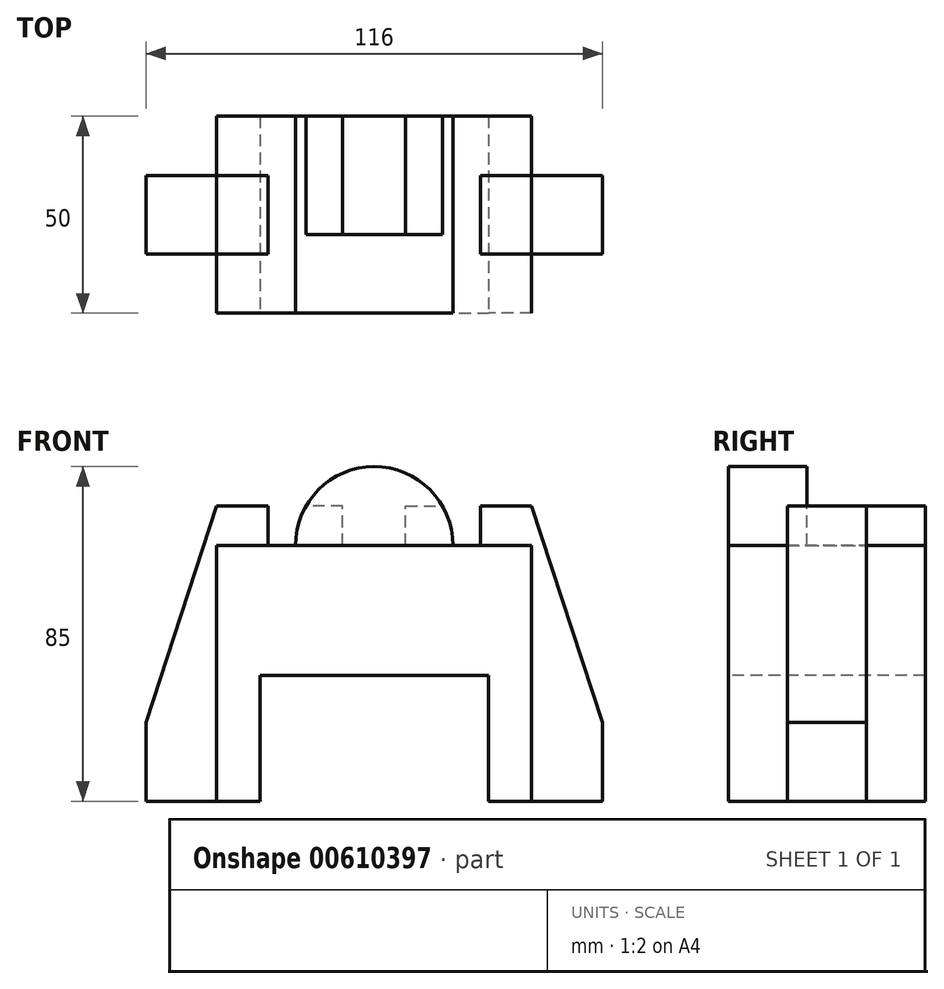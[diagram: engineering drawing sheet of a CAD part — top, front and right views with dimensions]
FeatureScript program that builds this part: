
annotation { "Feature Type Name" : "Feature", "Feature Type Description" : "" }
export const myFeature = defineFeature(function(context is Context, id is Id, definition is map)
    precondition{}
    {
        {
            var Q0;
            Q0=qCreatedBy(makeId("Top.planeOp"),FACE);
            var sketch = newSketch(context, id + "F0", { "sketchPlane" : qUnion([Q0])});
            skLineSegment(sketch, "E0.bottom", {"start": v(40, 25) * mm, "end": v(-40, 25) * mm});
            skLineSegment(sketch, "E0.top", {"start": v(40, -25) * mm, "end": v(-40, -25) * mm});
            skLineSegment(sketch, "E0.left", {"start": v(40, 25) * mm, "end": v(40, -25) * mm});
            skLineSegment(sketch, "E0.right", {"start": v(-40, 25) * mm, "end": v(-40, -25) * mm});
            skPoint(sketch, "E0.middle", {"position": v(0, 0) * mm});
            skSolve(sketch);
        }
        {
            var Q0;
            Q0 = qSketchRegion(id + "F0", true);
            extrude(context, id + "F1", {"entities" : qUnion([Q0]), "depth" : 65 * mm, "offsetDistance" : 25 * mm});
        }
        {
            var Q0;
            Q0=makeQuery(id+"F1.opExtrude","SWEPT_FACE",FACE,{"disambiguationData":[OSD([sQuery(id+"F0.wireOp",EDGE,"E0.top")])]});
            var sketch = newSketch(context, id + "F2", { "sketchPlane" : qUnion([Q0])});
            skLineSegment(sketch, "E1", {"start": v(0, 0) * mm, "end": v(29, 0) * mm});
            skLineSegment(sketch, "E2", {"start": v(29, 0) * mm, "end": v(-29, 0) * mm});
            skLineSegment(sketch, "E3", {"start": v(-29, 0) * mm, "end": v(-29, 32) * mm});
            skLineSegment(sketch, "E4", {"start": v(-29, 32) * mm, "end": v(29, 32) * mm});
            skLineSegment(sketch, "E5", {"start": v(29, 32) * mm, "end": v(29, 0) * mm});
            skSolve(sketch);
        }
        {
            var Q0;
            Q0 = qSketchRegion(id + "F2", true);
            extrude(context, id + "F3", {"entities" : qUnion([Q0]), "operationType" : NewBodyOperationType.REMOVE, "oppositeDirection" : true, "depth" : 234.7 * mm, "offsetDistance" : 25 * mm});
        }
        {
            var Q0;
            Q0=makeQuery(id+"F1.opExtrude","SWEPT_FACE",FACE,{"disambiguationData":[OSD([sQuery(id+"F0.wireOp",EDGE,"E0.top")])]});
            var sketch = newSketch(context, id + "F4", { "sketchPlane" : qUnion([Q0])});
            skArc(sketch, "E6", {"start": v(20, 65) * mm, "mid": v(0, 85) * mm, "end": v(-20, 65) * mm});
            skLineSegment(sketch, "E7", {"start": v(-36.6, 65) * mm, "end": v(34.21, 65) * mm});
            skSolve(sketch);
        }
        {
            var Q0;
            {var subQ0=sQuery(id+"F4.wireOp",EDGE,"E6");Q0=makeQuery(id+"F4.imprint","IMPRINT",FACE,{"disambiguationData":[TD([[makeQuery(id+"F4.imprint","IMPRINT",EDGE,{"derivedFrom":subQ0}),1.0]])]});}
            var Q1;
            Q1=makeQuery(id+"F1.opExtrude","SWEPT_FACE",FACE,{"disambiguationData":[OSD([sQuery(id+"F0.wireOp",EDGE,"E0.bottom")])]});
            extrude(context, id + "F5", {"entities" : qUnion([Q0]), "endBound" : BoundingType.UP_TO_SURFACE, "oppositeDirection" : true, "depth" : 25 * mm, "endBoundEntityFace" : qUnion([Q1]), "offsetDistance" : 25 * mm});
        }
        {
            var Q0;
            Q0=makeQuery(id+"F5.opExtrude","CAP_FACE",FACE,{"disambiguationData":[OSD([sQuery(id+"F4.wireOp",EDGE,"E6"),sQuery(id+"F4.wireOp",EDGE,"E7")])],"isStart":false});
            var sketch = newSketch(context, id + "F6", { "sketchPlane" : qUnion([Q0])});
            skLineSegment(sketch, "E8", {"start": v(0, 65) * mm, "end": v(8, 65) * mm});
            skLineSegment(sketch, "E9", {"start": v(8, 65) * mm, "end": v(-8, 65) * mm});
            skLineSegment(sketch, "E10", {"start": v(-8, 65) * mm, "end": v(-8, 75) * mm});
            skLineSegment(sketch, "E11", {"start": v(-8, 75) * mm, "end": v(-17.32, 75) * mm});
            skLineSegment(sketch, "E12", {"start": v(8, 65) * mm, "end": v(8, 75) * mm});
            skLineSegment(sketch, "E13", {"start": v(8, 75) * mm, "end": v(17.32, 75) * mm});
            skLineSegment(sketch, "E14", {"start": v(-8, 75) * mm, "end": v(8, 75) * mm});
            skSolve(sketch);
        }
        {
            var Q0;
            {var subQ0=sQuery(id+"F6.wireOp",EDGE,"E11");Q0=makeQuery(id+"F6.imprint","IMPRINT",FACE,{"disambiguationData":[TD([[makeQuery(id+"F6.imprint","IMPRINT",EDGE,{"derivedFrom":subQ0}),-1.0]])]});}
            var Q1;
            {var subQ5=sQuery(id+"F6.wireOp",EDGE,"E10");Q1=makeQuery(id+"F6.imprint","IMPRINT",FACE,{"disambiguationData":[TD([[makeQuery(id+"F6.imprint","IMPRINT",EDGE,{"derivedFrom":subQ5}),-1.0]])]});}
            extrude(context, id + "F7", {"entities" : qUnion([Q0, Q1]), "operationType" : NewBodyOperationType.REMOVE, "oppositeDirection" : true, "depth" : 30 * mm, "offsetDistance" : 25 * mm});
        }
        {
            var Q0;
            Q0=qCreatedBy(makeId("Front.planeOp"),FACE);
            var sketch = newSketch(context, id + "F8", { "sketchPlane" : qUnion([Q0])});
            skLineSegment(sketch, "E15.0.0", {"start": v(29, 0) * mm, "end": v(29, 32) * mm});
            skLineSegment(sketch, "E15.0.1", {"start": v(29, 32) * mm, "end": v(-29, 32) * mm});
            skLineSegment(sketch, "E15.0.2", {"start": v(-29, 32) * mm, "end": v(-29, 0) * mm});
            skLineSegment(sketch, "E15.0.3", {"start": v(-29, 0) * mm, "end": v(-40, 0) * mm});
            skLineSegment(sketch, "E15.0.4", {"start": v(-40, 0) * mm, "end": v(-40, 65) * mm});
            skLineSegment(sketch, "E15.0.5", {"start": v(-40, 65) * mm, "end": v(40, 65) * mm});
            skLineSegment(sketch, "E15.0.6", {"start": v(40, 65) * mm, "end": v(40, 0) * mm});
            skLineSegment(sketch, "E15.0.7", {"start": v(40, 0) * mm, "end": v(29, 0) * mm});
            skLineSegment(sketch, "E16", {"start": v(40, 0) * mm, "end": v(58, 0) * mm});
            skLineSegment(sketch, "E17", {"start": v(40, 65) * mm, "end": v(27, 65) * mm});
            skLineSegment(sketch, "E18", {"start": v(27, 65) * mm, "end": v(27, 75) * mm});
            skLineSegment(sketch, "E19", {"start": v(58, 0) * mm, "end": v(58, 20) * mm});
            skLineSegment(sketch, "E20", {"start": v(27, 75) * mm, "end": v(40, 75) * mm});
            skLineSegment(sketch, "E21", {"start": v(40, 75) * mm, "end": v(58, 20) * mm});
            skLineSegment(sketch, "E22.MirrorCS", {"start": v(-58, 0) * mm, "end": v(-58, 20) * mm});
            skLineSegment(sketch, "E23.MirrorCS", {"start": v(-40, 75) * mm, "end": v(-58, 20) * mm});
            skLineSegment(sketch, "E24.MirrorCS", {"start": v(-40, 0) * mm, "end": v(-58, 0) * mm});
            skLineSegment(sketch, "E25.MirrorCS", {"start": v(-27, 65) * mm, "end": v(-27, 75) * mm});
            skLineSegment(sketch, "E26.MirrorCS", {"start": v(-27, 75) * mm, "end": v(-40, 75) * mm});
            skSolve(sketch);
        }
        {
            var Q0;
            Q0=makeQuery(id+"F8.imprint","IMPRINT",FACE,{"disambiguationData":[TD([[makeQuery(id+"F8.imprint","IMPRINT",EDGE,{"derivedFrom":sQuery(id+"F8.wireOp",EDGE,"E15.0.6")}),1.0]])]});
            var Q1;
            {var subQ1=sQuery(id+"F8.wireOp",EDGE,"E15.0.4");Q1=makeQuery(id+"F8.imprint","IMPRINT",FACE,{"disambiguationData":[TD([[makeQuery(id+"F8.imprint","IMPRINT",EDGE,{"derivedFrom":subQ1}),1.0]])]});}
            extrude(context, id + "F9", {"entities" : qUnion([Q0, Q1]), "depth" : 10 * mm, "offsetDistance" : 25 * mm, "hasSecondDirection" : true, "secondDirectionOppositeDirection" : true, "secondDirectionDepth" : 10 * mm});
        }
    });
